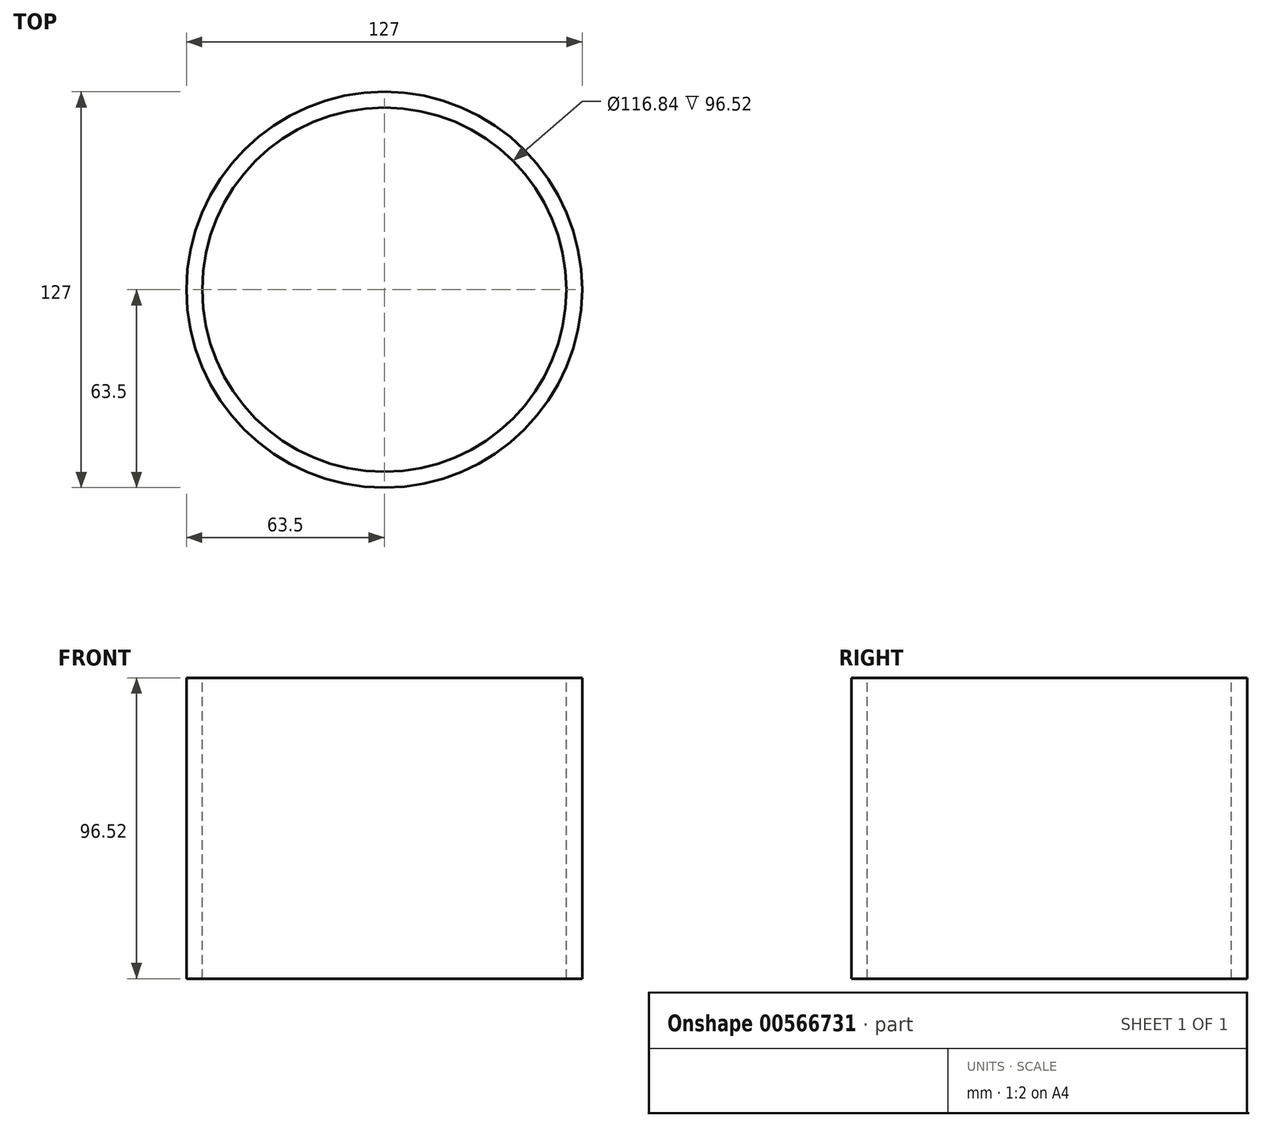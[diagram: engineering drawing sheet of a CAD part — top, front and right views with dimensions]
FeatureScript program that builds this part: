
annotation { "Feature Type Name" : "Feature", "Feature Type Description" : "" }
export const myFeature = defineFeature(function(context is Context, id is Id, definition is map)
    precondition{}
    {
        {
            var Q0;
            Q0=qCreatedBy(makeId("Top.planeOp"),FACE);
            var sketch = newSketch(context, id + "F0", { "sketchPlane" : qUnion([Q0])});
            skCircle(sketch, "E0", {"center": v(0, 0) * mm, "radius": 63.5 * mm});
            skSolve(sketch);
        }
        {
            var Q0;
            Q0 = qSketchRegion(id + "F0", true);
            extrude(context, id + "F1", {"entities" : qUnion([Q0]), "endBound" : BoundingType.SYMMETRIC, "depth" : 96.52 * mm, "offsetDistance" : 25.4 * mm});
        }
        {
            var Q0;
            Q0=qCreatedBy(makeId("Top.planeOp"),FACE);
            var sketch = newSketch(context, id + "F2", { "sketchPlane" : qUnion([Q0])});
            skCircle(sketch, "E1", {"center": v(0, 0) * mm, "radius": 58.42 * mm});
            skSolve(sketch);
        }
        {
            var Q0;
            Q0 = qSketchRegion(id + "F2", true);
            extrude(context, id + "F3", {"entities" : qUnion([Q0]), "operationType" : NewBodyOperationType.REMOVE, "endBound" : BoundingType.SYMMETRIC, "oppositeDirection" : true, "depth" : 101.6 * mm, "offsetDistance" : 25.4 * mm});
        }
    });
